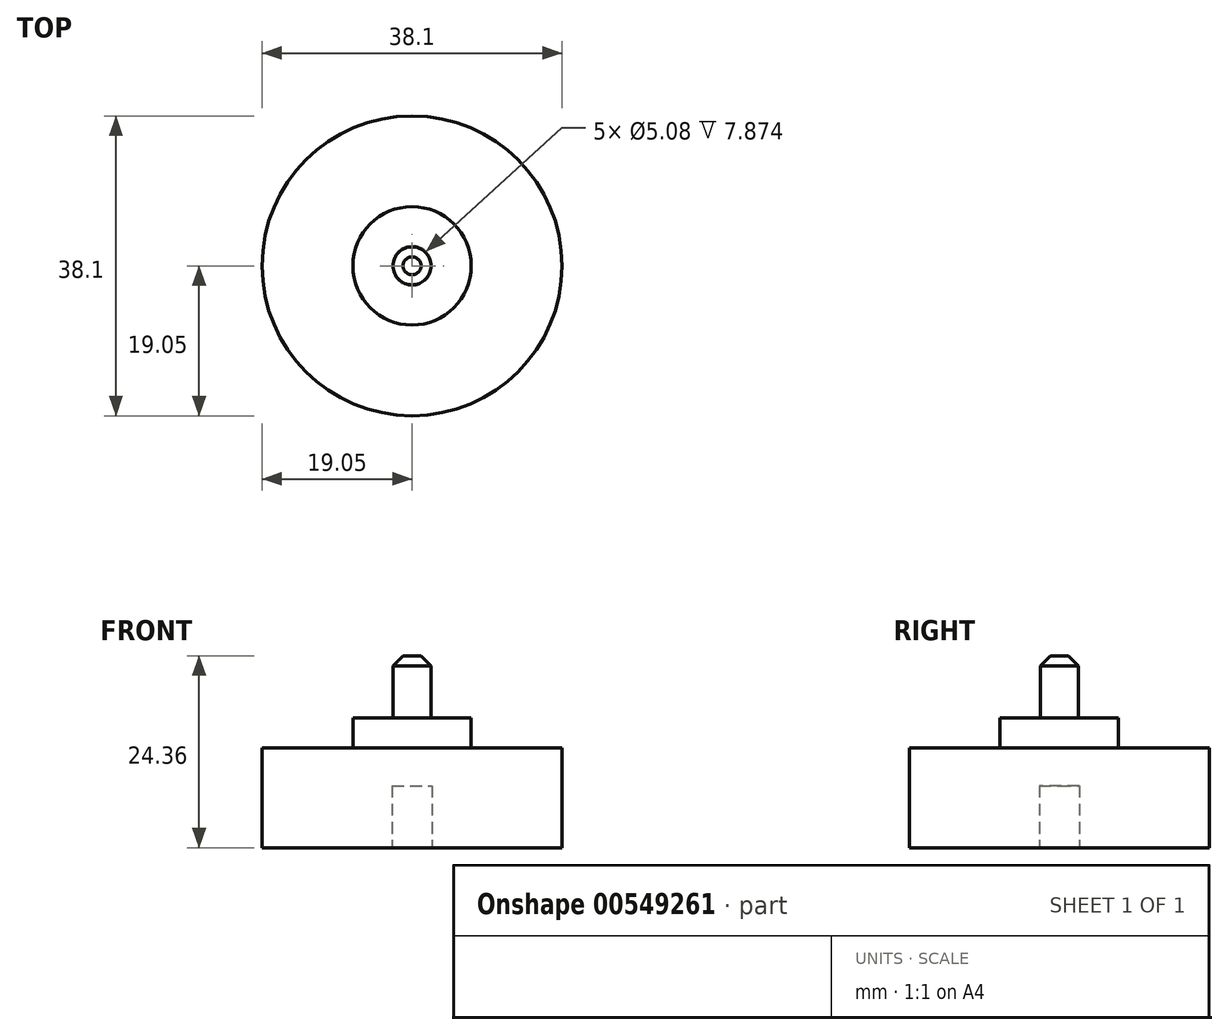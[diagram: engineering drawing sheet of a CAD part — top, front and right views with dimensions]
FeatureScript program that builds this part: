
annotation { "Feature Type Name" : "Feature", "Feature Type Description" : "" }
export const myFeature = defineFeature(function(context is Context, id is Id, definition is map)
    precondition{}
    {
        {
            var Q0;
            Q0=qCreatedBy(makeId("Front.planeOp"),FACE);
            var sketch = newSketch(context, id + "F0", { "sketchPlane" : qUnion([Q0])});
            skLineSegment(sketch, "E0", {"start": v(19.05, 0) * mm, "end": v(19.05, 12.7) * mm});
            skLineSegment(sketch, "E1", {"start": v(19.05, 12.7) * mm, "end": v(7.52, 12.7) * mm});
            skLineSegment(sketch, "E2", {"start": v(2.41, 16.5) * mm, "end": v(7.52, 16.5) * mm});
            skLineSegment(sketch, "E3", {"start": v(7.52, 16.5) * mm, "end": v(7.52, 12.7) * mm});
            skLineSegment(sketch, "E4", {"start": v(0, 24.36) * mm, "end": v(2.41, 24.36) * mm});
            skLineSegment(sketch, "E5", {"start": v(2.41, 24.36) * mm, "end": v(2.41, 16.5) * mm});
            skPoint(sketch, "E6.orphan", {"position": v(2.41, 12.7) * mm});
            skPoint(sketch, "E7.start.orphan", {"position": v(0, 12.7) * mm});
            skLineSegment(sketch, "E8", {"start": v(2.54, 0) * mm, "end": v(2.54, 7.87) * mm});
            skLineSegment(sketch, "E9", {"start": v(2.54, 7.87) * mm, "end": v(0, 7.87) * mm});
            skLineSegment(sketch, "E10", {"start": v(0, 7.87) * mm, "end": v(0, 24.36) * mm});
            skLineSegment(sketch, "E11", {"start": v(2.54, 0) * mm, "end": v(19.05, 0) * mm});
            skSolve(sketch);
        }
        {
            var Q0;
            Q0 = qSketchRegion(id + "F0", true);
            var Q1;
            Q1=sQuery(id+"F0.wireOp",EDGE,"E10");
            revolve(context, id + "F1", {"entities" : qUnion([Q0]), "axis" : qUnion([Q1]), "revolveType" : RevolveType.FULL});
        }
        {
            var Q0;
            Q0=makeQuery(id+"F1.opRevolve","SWEPT_EDGE",EDGE,{"disambiguationData":[OSD([sQuery(id+"F0.wireOp",EDGE,"E4"),sQuery(id+"F0.wireOp",EDGE,"E5")])]});
            chamfer(context, id + "F2", {"entities" : qUnion([Q0]), "width" : 1.27 * mm, "tangentPropagation" : true});
        }
    });
